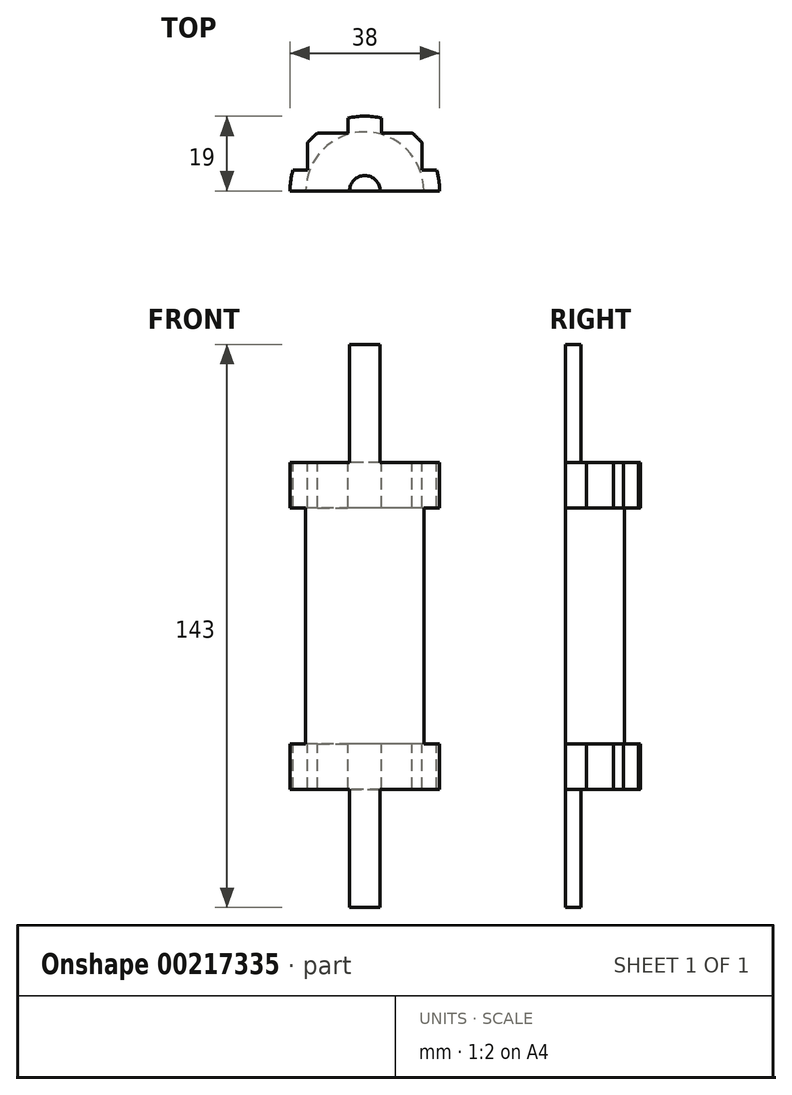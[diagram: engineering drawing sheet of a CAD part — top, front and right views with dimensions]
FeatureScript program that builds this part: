
annotation { "Feature Type Name" : "Feature", "Feature Type Description" : "" }
export const myFeature = defineFeature(function(context is Context, id is Id, definition is map)
    precondition{}
    {
        {
            var Q0;
            Q0=qCreatedBy(makeId("Top.planeOp"),FACE);
            var sketch = newSketch(context, id + "F0", { "sketchPlane" : qUnion([Q0])});
            skArc(sketch, "E0", {"start": v(19, 0) * mm, "mid": v(0, 19) * mm, "end": v(-19, 0) * mm});
            skLineSegment(sketch, "E1", {"start": v(-19, 0) * mm, "end": v(19, 0) * mm});
            skSolve(sketch);
        }
        {
            var Q0;
            Q0 = qSketchRegion(id + "F0", true);
            extrude(context, id + "F1", {"entities" : qUnion([Q0]), "endBound" : BoundingType.SYMMETRIC, "depth" : 83 * mm});
        }
        {
            var Q0;
            Q0=makeQuery(id+"F1.opExtrude","CAP_FACE",FACE,{"disambiguationData":[OSD([sQuery(id+"F0.wireOp",EDGE,"E0"),sQuery(id+"F0.wireOp",EDGE,"E1")])],"isStart":false});
            var sketch = newSketch(context, id + "F2", { "sketchPlane" : qUnion([Q0])});
            skArc(sketch, "E2", {"start": v(3.9, 0) * mm, "mid": v(0, 3.9) * mm, "end": v(-3.9, 0) * mm});
            skLineSegment(sketch, "E3", {"start": v(-3.9, 0) * mm, "end": v(3.9, 0) * mm});
            skSolve(sketch);
        }
        {
            var Q0;
            Q0 = qSketchRegion(id + "F2", true);
            extrude(context, id + "F3", {"entities" : qUnion([Q0]), "operationType" : NewBodyOperationType.ADD, "depth" : 30 * mm});
        }
        {
            var Q0;
            Q0=makeQuery(id+"F1.opExtrude","CAP_FACE",FACE,{"disambiguationData":[OSD([sQuery(id+"F0.wireOp",EDGE,"E0"),sQuery(id+"F0.wireOp",EDGE,"E1")])],"isStart":true});
            var sketch = newSketch(context, id + "F4", { "sketchPlane" : qUnion([Q0])});
            skArc(sketch, "E4", {"start": v(-3.9, 0) * mm, "mid": v(0, -3.9) * mm, "end": v(3.9, 0) * mm});
            skLineSegment(sketch, "E5", {"start": v(-3.9, 0) * mm, "end": v(3.9, 0) * mm});
            skSolve(sketch);
        }
        {
            var Q0;
            Q0=makeQuery(id+"F4.imprint","IMPRINT",FACE,{"disambiguationData":[TD([[makeQuery(id+"F4.imprint","IMPRINT",EDGE,{"derivedFrom":sQuery(id+"F4.wireOp",EDGE,"E4")}),1.0]])]});
            extrude(context, id + "F5", {"entities" : qUnion([Q0]), "operationType" : NewBodyOperationType.ADD, "depth" : 30 * mm});
        }
        {
            var Q0;
            Q0=makeQuery(id+"F1.opExtrude","CAP_FACE",FACE,{"disambiguationData":[OSD([sQuery(id+"F0.wireOp",EDGE,"E0"),sQuery(id+"F0.wireOp",EDGE,"E1")])],"isStart":false});
            var sketch = newSketch(context, id + "F6", { "sketchPlane" : qUnion([Q0])});
            skLineSegment(sketch, "E6", {"start": v(-4.26, 18.52) * mm, "end": v(-4.26, 14.72) * mm});
            skLineSegment(sketch, "E7", {"start": v(-4.26, 14.72) * mm, "end": v(-12, 14.72) * mm});
            skLineSegment(sketch, "E8", {"start": v(-14.57, 12.2) * mm, "end": v(-14.57, 5.37) * mm});
            skLineSegment(sketch, "E9", {"start": v(-14.57, 5.37) * mm, "end": v(-18.23, 5.37) * mm});
            skArc(sketch, "E10", {"start": v(-18.23, 5.37) * mm, "mid": v(-16.75, 8.97) * mm, "end": v(-14.57, 12.2) * mm});
            skArc(sketch, "E11", {"start": v(-12, 14.72) * mm, "mid": v(-8.35, 17.06) * mm, "end": v(-4.26, 18.52) * mm});
            skLineSegment(sketch, "E12.MirrorCS", {"start": v(4.26, 14.72) * mm, "end": v(12, 14.72) * mm});
            skLineSegment(sketch, "E13.MirrorCS", {"start": v(4.26, 18.52) * mm, "end": v(4.26, 14.72) * mm});
            skArc(sketch, "E14.MirrorCS", {"start": v(12, 14.72) * mm, "mid": v(8.35, 17.06) * mm, "end": v(4.26, 18.52) * mm});
            skArc(sketch, "E15.MirrorCS", {"start": v(18.23, 5.37) * mm, "mid": v(16.75, 8.97) * mm, "end": v(14.57, 12.2) * mm});
            skLineSegment(sketch, "E16.MirrorCS", {"start": v(14.57, 12.2) * mm, "end": v(14.57, 5.37) * mm});
            skLineSegment(sketch, "E17.MirrorCS", {"start": v(14.57, 5.37) * mm, "end": v(18.23, 5.37) * mm});
            skSolve(sketch);
        }
        {
            var Q0;
            Q0=makeQuery(id+"F6.imprint","IMPRINT",FACE,{"disambiguationData":[TD([[makeQuery(id+"F6.imprint","IMPRINT",EDGE,{"derivedFrom":sQuery(id+"F6.wireOp",EDGE,"E8")}),-1.0]])]});
            var Q1;
            Q1=makeQuery(id+"F6.imprint","IMPRINT",FACE,{"disambiguationData":[TD([[makeQuery(id+"F6.imprint","IMPRINT",EDGE,{"derivedFrom":sQuery(id+"F6.wireOp",EDGE,"E6")}),-1.0]])]});
            var Q2;
            Q2=makeQuery(id+"F6.imprint","IMPRINT",FACE,{"disambiguationData":[TD([[makeQuery(id+"F6.imprint","IMPRINT",EDGE,{"derivedFrom":sQuery(id+"F6.wireOp",EDGE,"E12.MirrorCS")}),1.0]])]});
            var Q3;
            Q3=makeQuery(id+"F6.imprint","IMPRINT",FACE,{"disambiguationData":[TD([[makeQuery(id+"F6.imprint","IMPRINT",EDGE,{"derivedFrom":sQuery(id+"F6.wireOp",EDGE,"E15.MirrorCS")}),1.0]])]});
            extrude(context, id + "F7", {"entities" : qUnion([Q0, Q1, Q2, Q3]), "operationType" : NewBodyOperationType.REMOVE, "endBound" : BoundingType.THROUGH_ALL, "oppositeDirection" : true, "depth" : 25 * mm});
        }
        {
            var Q0;
            Q0=qCreatedBy(makeId("Top.planeOp"),FACE);
            var sketch = newSketch(context, id + "F8", { "sketchPlane" : qUnion([Q0])});
            skArc(sketch, "E18", {"start": v(22.46, 0) * mm, "mid": v(0, 22.46) * mm, "end": v(-22.46, 0) * mm});
            skArc(sketch, "E19", {"start": v(15, 0) * mm, "mid": v(0, 15) * mm, "end": v(-15, 0) * mm});
            skLineSegment(sketch, "E20", {"start": v(-22.46, 0) * mm, "end": v(22.46, 0) * mm});
            skSolve(sketch);
        }
        {
            var Q0;
            {var subQ0=sQuery(id+"F8.wireOp",EDGE,"E18");Q0=makeQuery(id+"F8.imprint","IMPRINT",FACE,{"disambiguationData":[TD([[makeQuery(id+"F8.imprint","IMPRINT",EDGE,{"derivedFrom":subQ0}),1.0]])]});}
            extrude(context, id + "F9", {"entities" : qUnion([Q0]), "operationType" : NewBodyOperationType.REMOVE, "endBound" : BoundingType.SYMMETRIC, "oppositeDirection" : true, "depth" : 60 * mm});
        }
    });
